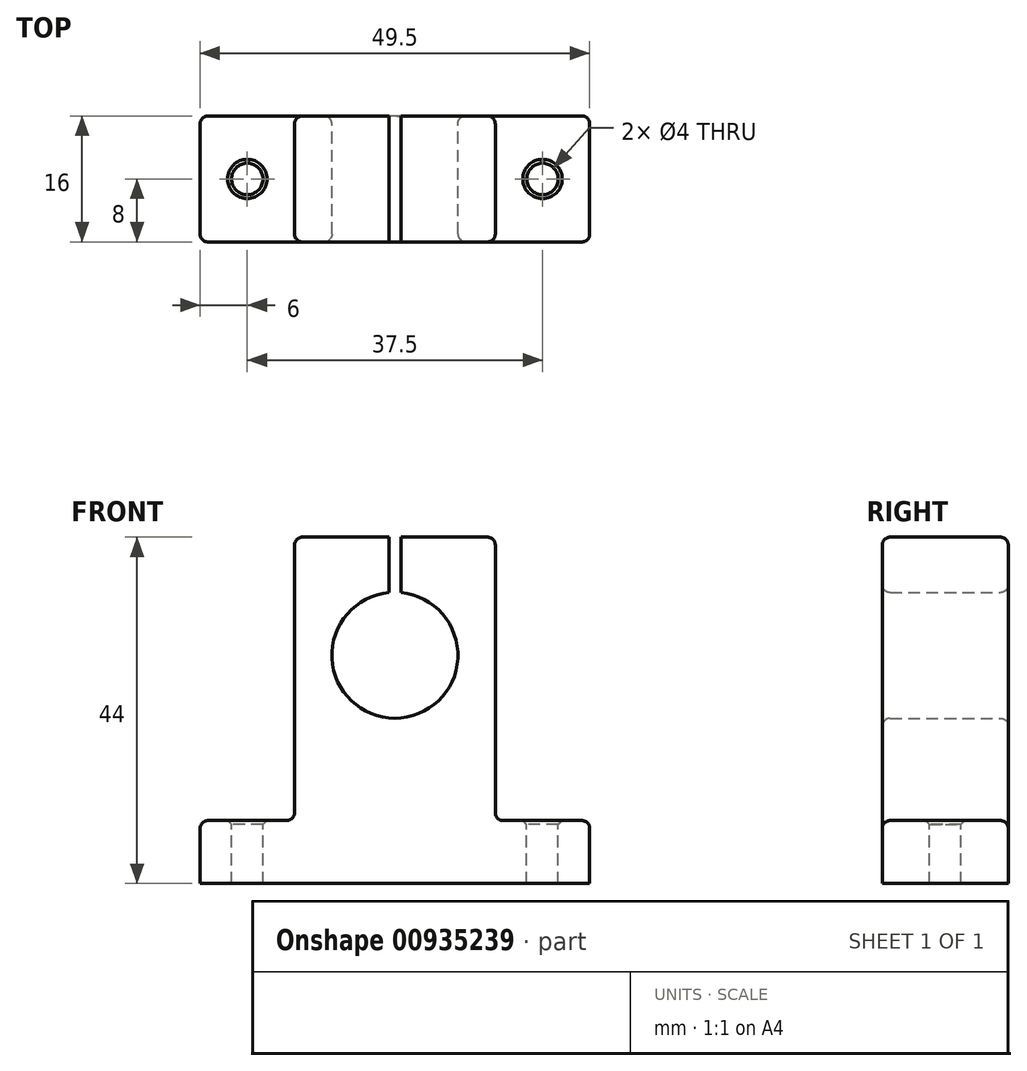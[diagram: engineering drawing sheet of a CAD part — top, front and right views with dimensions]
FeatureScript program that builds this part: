
annotation { "Feature Type Name" : "Feature", "Feature Type Description" : "" }
export const myFeature = defineFeature(function(context is Context, id is Id, definition is map)
    precondition{}
    {
        {
            assignVariable(context, id + "F0", {"name" : "teste", "anyValue" : 16});
        }
        {
            var Q0;
            Q0=qCreatedBy(makeId("Front.planeOp"),FACE);
            var sketch = newSketch(context, id + "F1", { "sketchPlane" : qUnion([Q0])});
            skLineSegment(sketch, "E0", {"start": v(24.75, -11.03) * mm, "end": v(-24.75, -11.03) * mm});
            skLineSegment(sketch, "E1", {"start": v(-24.75, -11.03) * mm, "end": v(-24.75, -3.03) * mm});
            skLineSegment(sketch, "E2", {"start": v(-24.75, -3.03) * mm, "end": v(-12.75, -3.03) * mm});
            skLineSegment(sketch, "E3", {"start": v(-12.75, -3.03) * mm, "end": v(-12.75, 32.97) * mm});
            skLineSegment(sketch, "E4", {"start": v(-12.75, 32.97) * mm, "end": v(-0.75, 32.97) * mm});
            skLineSegment(sketch, "E5", {"start": v(12.75, 32.97) * mm, "end": v(12.75, -3.03) * mm});
            skLineSegment(sketch, "E6", {"start": v(12.75, -3.03) * mm, "end": v(24.75, -3.03) * mm});
            skLineSegment(sketch, "E7", {"start": v(24.75, -3.03) * mm, "end": v(24.75, -11.03) * mm});
            skLineSegment(sketch, "E8", {"start": v(0, -17.71) * mm, "end": v(0, 26.6) * mm, "construction": true});
            skArc(sketch, "E9", {"start": v(-0.75, 25.93) * mm, "mid": v(0, 9.97) * mm, "end": v(0.75, 25.93) * mm});
            skLineSegment(sketch, "E10", {"start": v(-0.75, 32.97) * mm, "end": v(-0.75, 25.93) * mm});
            skLineSegment(sketch, "E11", {"start": v(0.75, 32.97) * mm, "end": v(0.75, 25.93) * mm});
            skLineSegment(sketch, "E12.trimOffspring", {"start": v(0.75, 32.97) * mm, "end": v(12.75, 32.97) * mm});
            skSolve(sketch);
        }
        {
            var Q0;
            Q0=makeQuery(id+"F1.imprint","IMPRINT",FACE,{"disambiguationData":[TD([[makeQuery(id+"F1.imprint","IMPRINT",EDGE,{"derivedFrom":sQuery(id+"F1.wireOp",EDGE,"E0")}),-1.0]])]});
            extrude(context, id + "F2", {"entities" : qUnion([Q0]), "depth" : (getVariable(context, 'teste')) * mm, "offsetDistance" : 25 * mm});
        }
        {
            var Q0;
            Q0=makeQuery(id+"F2.opExtrude","SWEPT_FACE",FACE,{"disambiguationData":[OSD([sQuery(id+"F1.wireOp",EDGE,"E6")])]});
            var sketch = newSketch(context, id + "F3", { "sketchPlane" : qUnion([Q0])});
            skPoint(sketch, "E13", {"position": v(18.75, -8) * mm});
            skPoint(sketch, "E13.positionSnap0", {"position": v(12.75, -8) * mm});
            skPoint(sketch, "E13.positionSnap1", {"position": v(18.75, 0) * mm});
            skLineSegment(sketch, "E14", {"start": v(0, 3.6) * mm, "end": v(0, 10.93) * mm, "construction": true});
            skPoint(sketch, "E15.MirrorP", {"position": v(-18.75, -8) * mm});
            skSolve(sketch);
        }
        {
            var Q0;
            Q0=sQuery(id+"F3.wireOp",VERTEX,"E15.MirrorP");
            var Q1;
            Q1=sQuery(id+"F3.wireOp",VERTEX,"E13");
            var Q2;
            Q2=makeQuery(id+"F2.opExtrude","SWEPT_BODY",BODY,{"disambiguationData":[OSD([sQuery(id+"F1.wireOp",EDGE,"E0"),sQuery(id+"F1.wireOp",EDGE,"E1"),sQuery(id+"F1.wireOp",EDGE,"E2"),sQuery(id+"F1.wireOp",EDGE,"E3"),sQuery(id+"F1.wireOp",EDGE,"E4"),sQuery(id+"F1.wireOp",EDGE,"E5"),sQuery(id+"F1.wireOp",EDGE,"E6"),sQuery(id+"F1.wireOp",EDGE,"E7"),sQuery(id+"F1.wireOp",EDGE,"E9"),sQuery(id+"F1.wireOp",EDGE,"E10"),sQuery(id+"F1.wireOp",EDGE,"E11"),sQuery(id+"F1.wireOp",EDGE,"E12.trimOffspring")])]});
            hole(context, id + "F4", {"style" : HoleStyle.C_SINK, "endStyle" : HoleEndStyle.THROUGH, "holeDiameter" : 4 * mm, "cSinkDiameter" : 5 * mm, "cSinkAngle" : 90 * degree, "majorDiameter" : 5 * mm, "isTappedThrough" : true, "tappedDepth" : 12 * mm, "tapClearance" : 3, "locations" : qUnion([Q0, Q1]), "scope" : qUnion([Q2])});
        }
        {
            var Q0;
            Q0=makeQuery(id+"F2.opExtrude","CAP_EDGE",EDGE,{"disambiguationData":[OSD([sQuery(id+"F1.wireOp",EDGE,"E3")])],"isStart":false});
            var Q1;
            Q1=makeQuery(id+"F2.opExtrude","CAP_EDGE",EDGE,{"disambiguationData":[OSD([sQuery(id+"F1.wireOp",EDGE,"E4")])],"isStart":false});
            var Q2;
            Q2=makeQuery(id+"F2.opExtrude","CAP_EDGE",EDGE,{"disambiguationData":[OSD([sQuery(id+"F1.wireOp",EDGE,"E12.trimOffspring")])],"isStart":false});
            var Q3;
            Q3=makeQuery(id+"F2.opExtrude","CAP_EDGE",EDGE,{"disambiguationData":[OSD([sQuery(id+"F1.wireOp",EDGE,"E5")])],"isStart":false});
            var Q4;
            Q4=makeQuery(id+"F2.opExtrude","CAP_EDGE",EDGE,{"disambiguationData":[OSD([sQuery(id+"F1.wireOp",EDGE,"E6")])],"isStart":false});
            var Q5;
            Q5=makeQuery(id+"F2.opExtrude","CAP_EDGE",EDGE,{"disambiguationData":[OSD([sQuery(id+"F1.wireOp",EDGE,"E7")])],"isStart":false});
            var Q6;
            Q6=makeQuery(id+"F2.opExtrude","SWEPT_EDGE",EDGE,{"disambiguationData":[OSD([sQuery(id+"F1.wireOp",EDGE,"E6"),sQuery(id+"F1.wireOp",EDGE,"E7")])]});
            var Q7;
            Q7=makeQuery(id+"F2.opExtrude","CAP_EDGE",EDGE,{"disambiguationData":[OSD([sQuery(id+"F1.wireOp",EDGE,"E7")])],"isStart":true});
            var Q8;
            Q8=makeQuery(id+"F2.opExtrude","CAP_EDGE",EDGE,{"disambiguationData":[OSD([sQuery(id+"F1.wireOp",EDGE,"E6")])],"isStart":true});
            var Q9;
            Q9=makeQuery(id+"F2.opExtrude","SWEPT_EDGE",EDGE,{"disambiguationData":[OSD([sQuery(id+"F1.wireOp",EDGE,"E5"),sQuery(id+"F1.wireOp",EDGE,"E6")])]});
            var Q10;
            Q10=makeQuery(id+"F2.opExtrude","CAP_EDGE",EDGE,{"disambiguationData":[OSD([sQuery(id+"F1.wireOp",EDGE,"E5")])],"isStart":true});
            var Q11;
            Q11=makeQuery(id+"F2.opExtrude","SWEPT_EDGE",EDGE,{"disambiguationData":[OSD([sQuery(id+"F1.wireOp",EDGE,"E5"),sQuery(id+"F1.wireOp",EDGE,"E12.trimOffspring")])]});
            var Q12;
            Q12=makeQuery(id+"F2.opExtrude","CAP_EDGE",EDGE,{"disambiguationData":[OSD([sQuery(id+"F1.wireOp",EDGE,"E12.trimOffspring")])],"isStart":true});
            var Q13;
            Q13=makeQuery(id+"F2.opExtrude","CAP_EDGE",EDGE,{"disambiguationData":[OSD([sQuery(id+"F1.wireOp",EDGE,"E4")])],"isStart":true});
            var Q14;
            Q14=makeQuery(id+"F2.opExtrude","SWEPT_EDGE",EDGE,{"disambiguationData":[OSD([sQuery(id+"F1.wireOp",EDGE,"E3"),sQuery(id+"F1.wireOp",EDGE,"E4")])]});
            var Q15;
            Q15=makeQuery(id+"F2.opExtrude","CAP_EDGE",EDGE,{"disambiguationData":[OSD([sQuery(id+"F1.wireOp",EDGE,"E2")])],"isStart":false});
            var Q16;
            Q16=makeQuery(id+"F2.opExtrude","CAP_EDGE",EDGE,{"disambiguationData":[OSD([sQuery(id+"F1.wireOp",EDGE,"E1")])],"isStart":false});
            var Q17;
            Q17=makeQuery(id+"F2.opExtrude","SWEPT_EDGE",EDGE,{"disambiguationData":[OSD([sQuery(id+"F1.wireOp",EDGE,"E1"),sQuery(id+"F1.wireOp",EDGE,"E2")])]});
            var Q18;
            Q18=makeQuery(id+"F2.opExtrude","CAP_EDGE",EDGE,{"disambiguationData":[OSD([sQuery(id+"F1.wireOp",EDGE,"E9")])],"isStart":false});
            var Q19;
            Q19=makeQuery(id+"F2.opExtrude","CAP_EDGE",EDGE,{"disambiguationData":[OSD([sQuery(id+"F1.wireOp",EDGE,"E3")])],"isStart":true});
            var Q20;
            Q20=makeQuery(id+"F2.opExtrude","CAP_EDGE",EDGE,{"disambiguationData":[OSD([sQuery(id+"F1.wireOp",EDGE,"E9")])],"isStart":true});
            var Q21;
            Q21=makeQuery(id+"F2.opExtrude","SWEPT_EDGE",EDGE,{"disambiguationData":[OSD([sQuery(id+"F1.wireOp",EDGE,"E2"),sQuery(id+"F1.wireOp",EDGE,"E3")])]});
            var Q22;
            Q22=makeQuery(id+"F2.opExtrude","CAP_EDGE",EDGE,{"disambiguationData":[OSD([sQuery(id+"F1.wireOp",EDGE,"E2")])],"isStart":true});
            var Q23;
            Q23=makeQuery(id+"F2.opExtrude","CAP_EDGE",EDGE,{"disambiguationData":[OSD([sQuery(id+"F1.wireOp",EDGE,"E1")])],"isStart":true});
            fillet(context, id + "F5", {"entities" : qUnion([Q0, Q1, Q2, Q3, Q4, Q5, Q6, Q7, Q8, Q9, Q10, Q11, Q12, Q13, Q14, Q15, Q16, Q17, Q18, Q19, Q20, Q21, Q22, Q23]), "radius" : 1 * mm, "tangentPropagation" : true, "allowEdgeOverflow" : false});
        }
    });
